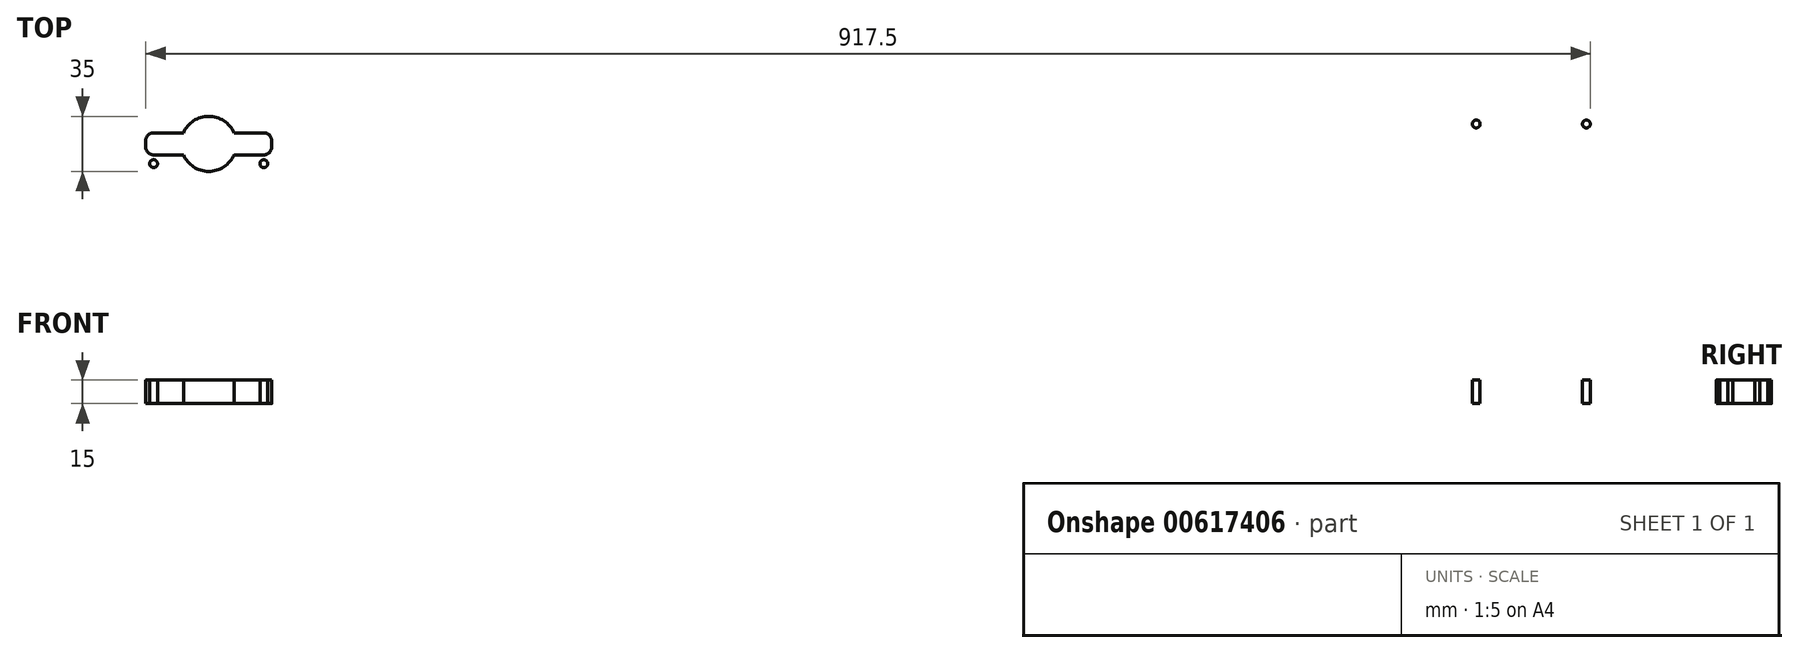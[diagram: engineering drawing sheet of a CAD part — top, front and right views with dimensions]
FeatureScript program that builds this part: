
annotation { "Feature Type Name" : "Feature", "Feature Type Description" : "" }
export const myFeature = defineFeature(function(context is Context, id is Id, definition is map)
    precondition{}
    {
        {
            var Q0;
            Q0=qCreatedBy(makeId("Top.planeOp"),FACE);
            var sketch = newSketch(context, id + "F0", { "sketchPlane" : qUnion([Q0])});
            skFitSpline(sketch, "E0", {"points": [v(-520, 0) * mm, v(-516.46, 43.08) * mm, v(-507.62, 67.7) * mm, v(-484.5, 75.83) * mm], "startDerivative": vector(0, 120.73) * mm, "endDerivative": vector(118.58, 4.94) * mm});
            skFitSpline(sketch, "E1", {"points": [v(-484.21, 75.83) * mm, v(-374.02, 75.83) * mm, v(-290.22, 70.2) * mm, v(-275.46, 75.83) * mm, v(-263.42, 111.83) * mm, v(-244.45, 126.4) * mm, v(-172.33, 130) * mm], "startDerivative": vector(441.53, 3.62) * mm, "endDerivative": vector(407.47, 0) * mm});
            skFitSpline(sketch, "E2", {"points": [v(-172.33, 130) * mm, v(-87.73, 119.26) * mm, v(0, 109.75) * mm], "startDerivative": vector(169.83, -22.35) * mm, "endDerivative": vector(214.4, 7.38) * mm});
            skFitSpline(sketch, "E3.MirrorCS", {"points": [v(-484.18, -75.83) * mm, v(-374.02, -75.83) * mm, v(-290.22, -70.2) * mm, v(-275.46, -75.83) * mm, v(-263.42, -111.83) * mm, v(-244.45, -126.4) * mm, v(-172.33, -130) * mm], "startDerivative": vector(441.53, -3.62) * mm, "endDerivative": vector(407.47, 0) * mm});
            skFitSpline(sketch, "E4.MirrorCS", {"points": [v(-520, 0) * mm, v(-516.46, -43.08) * mm, v(-507.62, -67.7) * mm, v(-484.5, -75.83) * mm], "startDerivative": vector(0, -120.73) * mm, "endDerivative": vector(118.58, -4.94) * mm});
            skFitSpline(sketch, "E5.MirrorCS", {"points": [v(-172.33, -130) * mm, v(-87.73, -119.26) * mm, v(0, -109.75) * mm], "startDerivative": vector(169.83, 22.35) * mm, "endDerivative": vector(214.4, -7.38) * mm});
            skFitSpline(sketch, "E6.MirrorCS", {"points": [v(-484.18, -75.83) * mm, v(-374.02, -75.83) * mm, v(-290.22, -70.2) * mm, v(-275.46, -75.83) * mm, v(-263.42, -111.83) * mm, v(-244.45, -126.4) * mm, v(-172.33, -130) * mm], "startDerivative": vector(441.53, -3.62) * mm, "endDerivative": vector(407.47, 0) * mm});
            skLineSegment(sketch, "E7", {"start": v(0, 192.92) * mm, "end": v(0, -277.29) * mm, "construction": true});
            skFitSpline(sketch, "E8.MirrorCS", {"points": [v(520, 0) * mm, v(516.46, 43.08) * mm, v(507.62, 67.7) * mm, v(484.5, 75.83) * mm], "startDerivative": vector(0, 120.73) * mm, "endDerivative": vector(-118.58, 4.94) * mm});
            skFitSpline(sketch, "E9.MirrorCS", {"points": [v(520, 0) * mm, v(516.46, -43.08) * mm, v(507.62, -67.7) * mm, v(484.5, -75.83) * mm], "startDerivative": vector(0, -120.73) * mm, "endDerivative": vector(-118.58, -4.94) * mm});
            skFitSpline(sketch, "E10.MirrorCS", {"points": [v(172.33, -130) * mm, v(87.73, -119.26) * mm, v(0, -109.75) * mm], "startDerivative": vector(-169.83, 22.35) * mm, "endDerivative": vector(-214.4, -7.38) * mm});
            skFitSpline(sketch, "E11.MirrorCS", {"points": [v(484.18, -75.83) * mm, v(374.02, -75.83) * mm, v(290.22, -70.2) * mm, v(275.46, -75.83) * mm, v(263.42, -111.83) * mm, v(244.45, -126.4) * mm, v(172.33, -130) * mm], "startDerivative": vector(-441.53, -3.62) * mm, "endDerivative": vector(-407.47, 0) * mm});
            skFitSpline(sketch, "E12.MirrorCS", {"points": [v(172.33, 130) * mm, v(87.73, 119.26) * mm, v(0, 109.75) * mm], "startDerivative": vector(-169.83, -22.35) * mm, "endDerivative": vector(-214.4, 7.38) * mm});
            skFitSpline(sketch, "E13.MirrorCS", {"points": [v(484.21, 75.83) * mm, v(374.02, 75.83) * mm, v(290.22, 70.2) * mm, v(275.46, 75.83) * mm, v(263.42, 111.83) * mm, v(244.45, 126.4) * mm, v(172.33, 130) * mm], "startDerivative": vector(-441.53, 3.62) * mm, "endDerivative": vector(-407.47, 0) * mm});
            skLineSegment(sketch, "E14", {"start": v(-484.21, 75.83) * mm, "end": v(-484.5, 75.83) * mm});
            skLineSegment(sketch, "E15", {"start": v(-484.18, -75.83) * mm, "end": v(-484.5, -75.83) * mm});
            skLineSegment(sketch, "E16", {"start": v(484.21, 75.83) * mm, "end": v(484.5, 75.83) * mm});
            skLineSegment(sketch, "E17", {"start": v(484.18, -75.83) * mm, "end": v(484.5, -75.83) * mm});
            skSolve(sketch);
        }
        {
            var Q0;
            Q0=makeQuery(id+"F0.imprint","IMPRINT",FACE,{"disambiguationData":[TD([[makeQuery(id+"F0.imprint","IMPRINT",EDGE,{"derivedFrom":sQuery(id+"F0.wireOp",EDGE,"E0")}),-1.0]])]});
            extrude(context, id + "F1", {"entities" : qUnion([Q0]), "depth" : 15 * mm, "offsetDistance" : 25 * mm});
        }
        {
            var Q0;
            Q0=makeQuery(id+"F1.opExtrude","CAP_FACE",FACE,{"disambiguationData":[OSD([sQuery(id+"F0.wireOp",EDGE,"E0"),sQuery(id+"F0.wireOp",EDGE,"E1"),sQuery(id+"F0.wireOp",EDGE,"E2"),sQuery(id+"F0.wireOp",EDGE,"E4.MirrorCS"),sQuery(id+"F0.wireOp",EDGE,"E5.MirrorCS"),sQuery(id+"F0.wireOp",EDGE,"E6.MirrorCS"),sQuery(id+"F0.wireOp",EDGE,"E8.MirrorCS"),sQuery(id+"F0.wireOp",EDGE,"E9.MirrorCS"),sQuery(id+"F0.wireOp",EDGE,"E10.MirrorCS"),sQuery(id+"F0.wireOp",EDGE,"E11.MirrorCS"),sQuery(id+"F0.wireOp",EDGE,"E12.MirrorCS"),sQuery(id+"F0.wireOp",EDGE,"E13.MirrorCS"),sQuery(id+"F0.wireOp",EDGE,"E14"),sQuery(id+"F0.wireOp",EDGE,"E15"),sQuery(id+"F0.wireOp",EDGE,"E16"),sQuery(id+"F0.wireOp",EDGE,"E17")])],"isStart":false});
            var sketch = newSketch(context, id + "F2", { "sketchPlane" : qUnion([Q0])});
            skLineSegment(sketch, "E18", {"start": v(520, 0) * mm, "end": v(420, 0) * mm, "construction": true});
            skArc(sketch, "E19", {"start": v(403.96, -7) * mm, "mid": v(420, -17.5) * mm, "end": v(436.04, -7) * mm});
            skLineSegment(sketch, "E20", {"start": v(380, 2) * mm, "end": v(380, -2) * mm});
            skLineSegment(sketch, "E21", {"start": v(460, -2) * mm, "end": v(460, 2) * mm});
            skLineSegment(sketch, "E22", {"start": v(385, 7) * mm, "end": v(403.96, 7) * mm});
            skLineSegment(sketch, "E23", {"start": v(455, -7) * mm, "end": v(436.04, -7) * mm});
            skLineSegment(sketch, "E24.trimOffspring", {"start": v(436.04, 7) * mm, "end": v(455, 7) * mm});
            skArc(sketch, "E25.trimOffspring", {"start": v(436.04, 7) * mm, "mid": v(420, 17.5) * mm, "end": v(403.96, 7) * mm});
            skPoint(sketch, "E26.end.orphan", {"position": v(420, 7) * mm});
            skLineSegment(sketch, "E27.trimOffspring", {"start": v(403.96, -7) * mm, "end": v(385, -7) * mm});
            skPoint(sketch, "E28.visualSharp", {"position": v(460, 7) * mm});
            skArc(sketch, "E28.filletArc", {"start": v(460, 2) * mm, "mid": v(458.54, 5.54) * mm, "end": v(455, 7) * mm});
            skPoint(sketch, "E29.visualSharp", {"position": v(460, -7) * mm});
            skArc(sketch, "E29.filletArc", {"start": v(455, -7) * mm, "mid": v(458.54, -5.54) * mm, "end": v(460, -2) * mm});
            skPoint(sketch, "E30.visualSharp", {"position": v(380, 7) * mm});
            skArc(sketch, "E30.filletArc", {"start": v(385, 7) * mm, "mid": v(381.46, 5.54) * mm, "end": v(380, 2) * mm});
            skPoint(sketch, "E31.visualSharp", {"position": v(380, -7) * mm});
            skArc(sketch, "E31.filletArc", {"start": v(380, -2) * mm, "mid": v(381.46, -5.54) * mm, "end": v(385, -7) * mm});
            skLineSegment(sketch, "E32", {"start": v(0, 167.8) * mm, "end": v(0, -153.78) * mm, "construction": true});
            skArc(sketch, "E33.MirrorCS", {"start": v(-403.96, -7) * mm, "mid": v(-420, -17.5) * mm, "end": v(-436.04, -7) * mm});
            skArc(sketch, "E34.MirrorCS", {"start": v(-436.04, 7) * mm, "mid": v(-420, 17.5) * mm, "end": v(-403.96, 7) * mm});
            skLineSegment(sketch, "E35.MirrorCS", {"start": v(-385, 7) * mm, "end": v(-403.96, 7) * mm});
            skLineSegment(sketch, "E36.MirrorCS", {"start": v(-403.96, -7) * mm, "end": v(-385, -7) * mm});
            skArc(sketch, "E37.MirrorCS", {"start": v(-385, 7) * mm, "mid": v(-381.46, 5.54) * mm, "end": v(-380, 2) * mm});
            skArc(sketch, "E38.MirrorCS", {"start": v(-380, -2) * mm, "mid": v(-381.46, -5.54) * mm, "end": v(-385, -7) * mm});
            skArc(sketch, "E39.MirrorCS", {"start": v(-460, 2) * mm, "mid": v(-458.54, 5.54) * mm, "end": v(-455, 7) * mm});
            skArc(sketch, "E40.MirrorCS", {"start": v(-455, -7) * mm, "mid": v(-458.54, -5.54) * mm, "end": v(-460, -2) * mm});
            skLineSegment(sketch, "E41.MirrorCS", {"start": v(-455, -7) * mm, "end": v(-436.04, -7) * mm});
            skLineSegment(sketch, "E42.MirrorCS", {"start": v(-436.04, 7) * mm, "end": v(-455, 7) * mm});
            skLineSegment(sketch, "E43", {"start": v(-460, 2) * mm, "end": v(-460, -2) * mm});
            skLineSegment(sketch, "E44", {"start": v(-380, 2) * mm, "end": v(-380, -2) * mm});
            skCircle(sketch, "E45", {"center": v(-385, 12.6) * mm, "radius": 2.5 * mm});
            skCircle(sketch, "E46", {"center": v(-455, 12.6) * mm, "radius": 2.5 * mm});
            skCircle(sketch, "E47.MirrorC", {"center": v(-385, -12.6) * mm, "radius": 2.5 * mm});
            skCircle(sketch, "E48.MirrorC", {"center": v(-455, -12.6) * mm, "radius": 2.5 * mm});
            skCircle(sketch, "E49.MirrorC", {"center": v(385, 12.6) * mm, "radius": 2.5 * mm});
            skCircle(sketch, "E50.MirrorC", {"center": v(385, -12.6) * mm, "radius": 2.5 * mm});
            skCircle(sketch, "E51.MirrorC", {"center": v(455, -12.6) * mm, "radius": 2.5 * mm});
            skCircle(sketch, "E52.MirrorC", {"center": v(455, 12.6) * mm, "radius": 2.5 * mm});
            skSolve(sketch);
        }
        {
            var Q0;
            Q0=makeQuery(id+"F2.imprint","IMPRINT",FACE,{"disambiguationData":[TD([[makeQuery(id+"F2.imprint","IMPRINT",EDGE,{"derivedFrom":sQuery(id+"F2.wireOp",EDGE,"E33.MirrorCS")}),-1.0]])]});
            var Q1;
            Q1=makeQuery(id+"F2.imprint","IMPRINT",FACE,{"disambiguationData":[TD([[makeQuery(id+"F2.imprint","IMPRINT",EDGE,{"derivedFrom":sQuery(id+"F2.wireOp",EDGE,"E19")}),1.0]])]});
            var Q2;
            Q2=makeQuery(id+"F2.imprint","IMPRINT",FACE,{"disambiguationData":[TD([[makeQuery(id+"F2.imprint","IMPRINT",EDGE,{"derivedFrom":sQuery(id+"F2.wireOp",EDGE,"E45")}),1.0]])]});
            var Q3;
            Q3=makeQuery(id+"F2.imprint","IMPRINT",FACE,{"disambiguationData":[TD([[makeQuery(id+"F2.imprint","IMPRINT",EDGE,{"derivedFrom":sQuery(id+"F2.wireOp",EDGE,"E47.MirrorC")}),-1.0]])]});
            var Q4;
            Q4=makeQuery(id+"F2.imprint","IMPRINT",FACE,{"disambiguationData":[TD([[makeQuery(id+"F2.imprint","IMPRINT",EDGE,{"derivedFrom":sQuery(id+"F2.wireOp",EDGE,"E48.MirrorC")}),-1.0]])]});
            var Q5;
            Q5=makeQuery(id+"F2.imprint","IMPRINT",FACE,{"disambiguationData":[TD([[makeQuery(id+"F2.imprint","IMPRINT",EDGE,{"derivedFrom":sQuery(id+"F2.wireOp",EDGE,"E46")}),1.0]])]});
            var Q6;
            Q6=makeQuery(id+"F2.imprint","IMPRINT",FACE,{"disambiguationData":[TD([[makeQuery(id+"F2.imprint","IMPRINT",EDGE,{"derivedFrom":sQuery(id+"F2.wireOp",EDGE,"E49.MirrorC")}),-1.0]])]});
            var Q7;
            Q7=makeQuery(id+"F2.imprint","IMPRINT",FACE,{"disambiguationData":[TD([[makeQuery(id+"F2.imprint","IMPRINT",EDGE,{"derivedFrom":sQuery(id+"F2.wireOp",EDGE,"E50.MirrorC")}),1.0]])]});
            var Q8;
            Q8=makeQuery(id+"F2.imprint","IMPRINT",FACE,{"disambiguationData":[TD([[makeQuery(id+"F2.imprint","IMPRINT",EDGE,{"derivedFrom":sQuery(id+"F2.wireOp",EDGE,"E52.MirrorC")}),-1.0]])]});
            var Q9;
            Q9=makeQuery(id+"F2.imprint","IMPRINT",FACE,{"disambiguationData":[TD([[makeQuery(id+"F2.imprint","IMPRINT",EDGE,{"derivedFrom":sQuery(id+"F2.wireOp",EDGE,"E51.MirrorC")}),1.0]])]});
            extrude(context, id + "F3", {"entities" : qUnion([Q0, Q1, Q2, Q3, Q4, Q5, Q6, Q7, Q8, Q9]), "operationType" : NewBodyOperationType.REMOVE, "oppositeDirection" : true, "depth" : 25 * mm, "offsetDistance" : 25 * mm});
        }
    });
